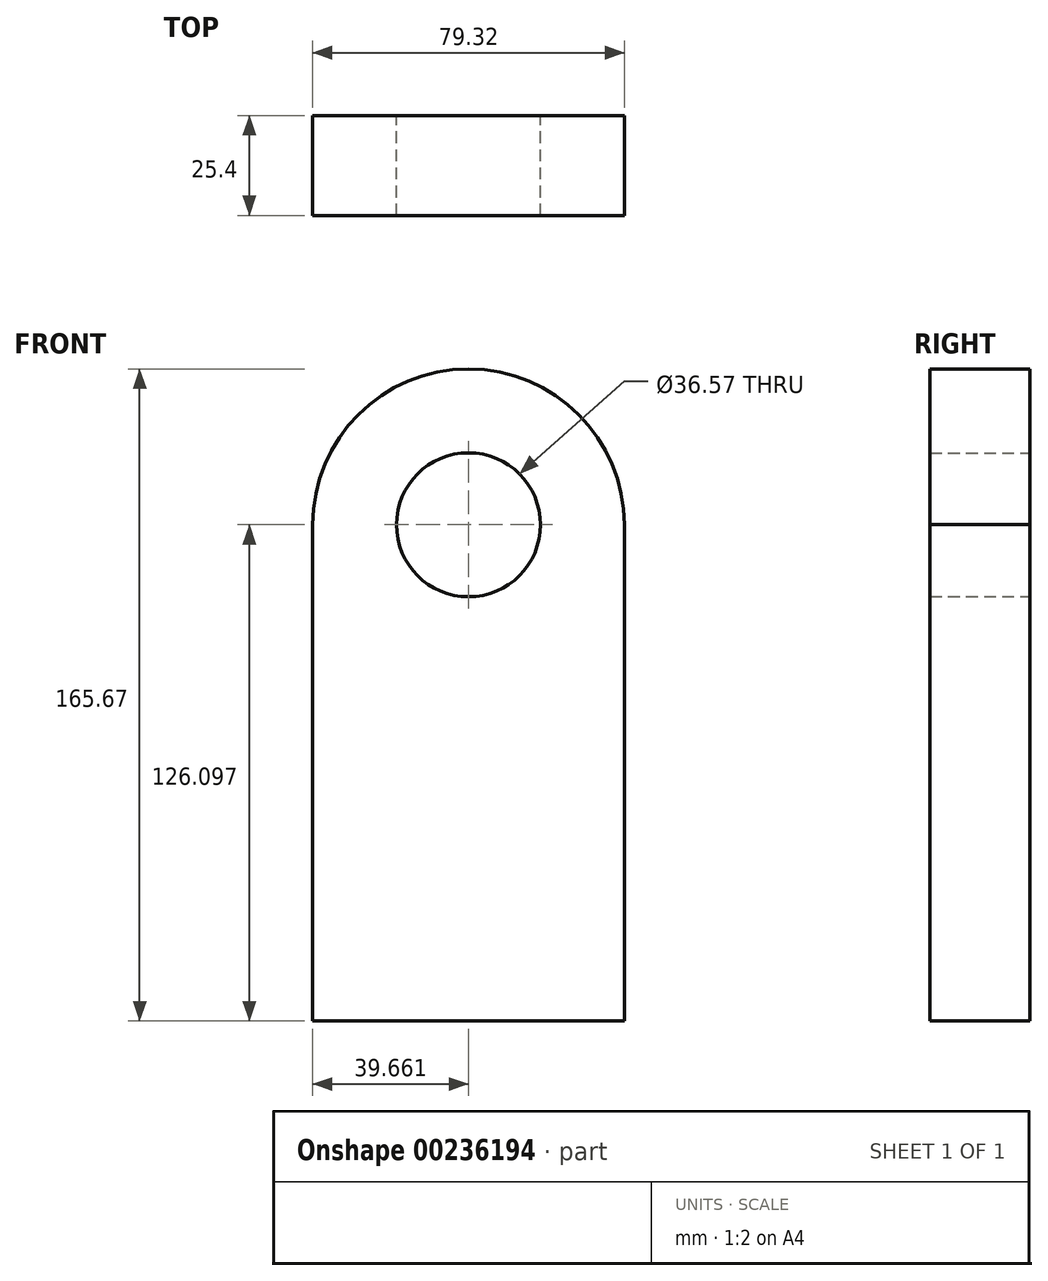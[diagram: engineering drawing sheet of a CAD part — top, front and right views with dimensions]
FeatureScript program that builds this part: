
annotation { "Feature Type Name" : "Feature", "Feature Type Description" : "" }
export const myFeature = defineFeature(function(context is Context, id is Id, definition is map)
    precondition{}
    {
        {
            var Q0;
            Q0=qCreatedBy(makeId("Front.planeOp"),FACE);
            var sketch = newSketch(context, id + "F0", { "sketchPlane" : qUnion([Q0])});
            skLineSegment(sketch, "E0.bottom", {"start": v(134.41, -29.41) * mm, "end": v(213.73, -29.41) * mm});
            skLineSegment(sketch, "E0.left", {"start": v(134.41, -29.41) * mm, "end": v(134.41, 96.69) * mm});
            skLineSegment(sketch, "E0.right", {"start": v(213.73, -29.41) * mm, "end": v(213.73, 96.69) * mm});
            skPoint(sketch, "E0.middle", {"position": v(174.07, 33.64) * mm});
            skArc(sketch, "E1", {"start": v(213.64, 96.69) * mm, "mid": v(174.07, 136.26) * mm, "end": v(134.5, 96.69) * mm});
            skCircle(sketch, "E2", {"center": v(174.07, 96.69) * mm, "radius": 18.28 * mm});
            skLineSegment(sketch, "E3", {"start": v(213.73, 96.69) * mm, "end": v(213.64, 96.69) * mm});
            skLineSegment(sketch, "E4.trimOffspring", {"start": v(134.5, 96.69) * mm, "end": v(134.41, 96.69) * mm});
            skSolve(sketch);
        }
        {
            var Q0;
            Q0=makeQuery(id+"F0.imprint","IMPRINT",FACE,{"disambiguationData":[TD([[makeQuery(id+"F0.imprint","IMPRINT",EDGE,{"derivedFrom":sQuery(id+"F0.wireOp",EDGE,"E0.bottom")}),1.0]])]});
            extrude(context, id + "F1", {"entities" : qUnion([Q0]), "depth" : 25.4 * mm});
        }
    });
